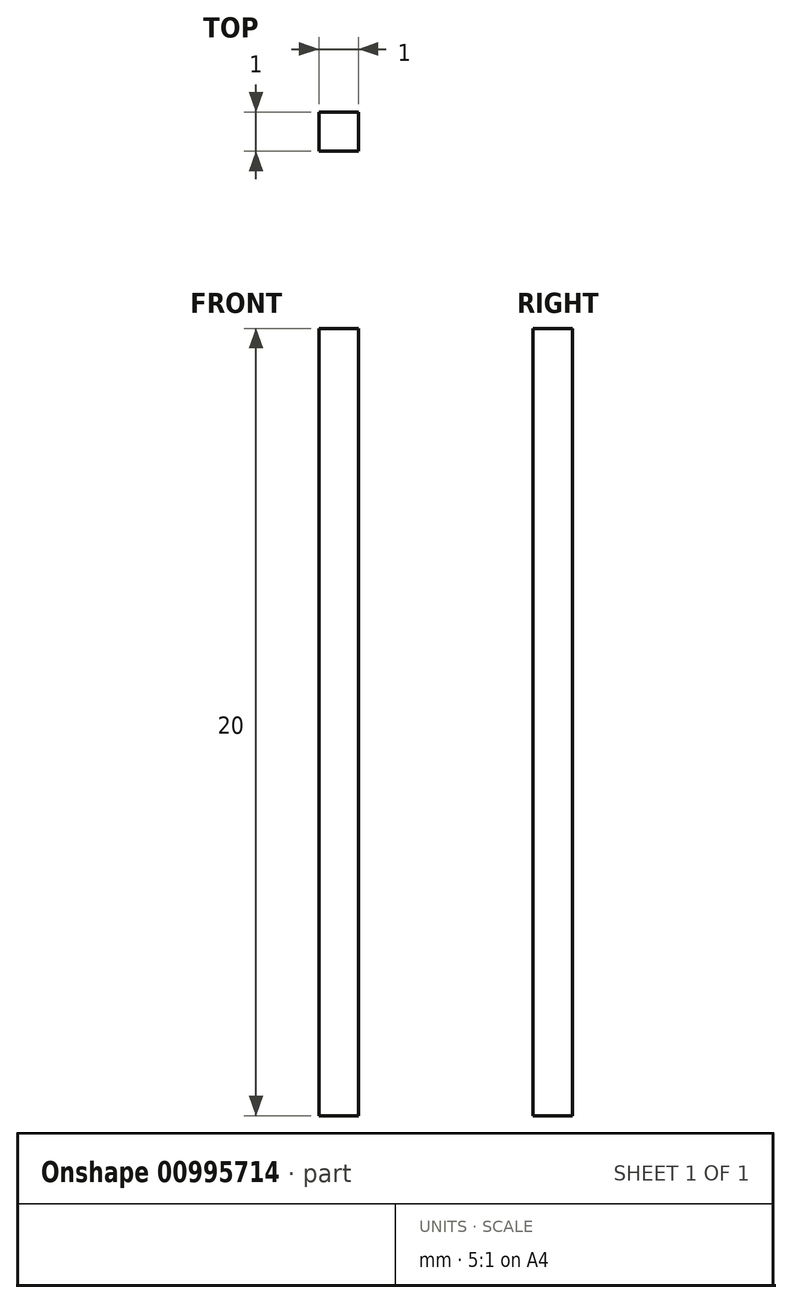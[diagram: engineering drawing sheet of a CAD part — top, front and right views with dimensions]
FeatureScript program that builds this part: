
annotation { "Feature Type Name" : "Feature", "Feature Type Description" : "" }
export const myFeature = defineFeature(function(context is Context, id is Id, definition is map)
    precondition{}
    {
        {
            var Q0;
            Q0=qCreatedBy(makeId("Top.planeOp"),FACE);
            var sketch = newSketch(context, id + "F0", { "sketchPlane" : qUnion([Q0])});
            skLineSegment(sketch, "E0.bottom", {"start": v(-0.5, -0.5) * mm, "end": v(0.5, -0.5) * mm});
            skLineSegment(sketch, "E0.top", {"start": v(-0.5, 0.5) * mm, "end": v(0.5, 0.5) * mm});
            skLineSegment(sketch, "E0.left", {"start": v(-0.5, -0.5) * mm, "end": v(-0.5, 0.5) * mm});
            skLineSegment(sketch, "E0.right", {"start": v(0.5, -0.5) * mm, "end": v(0.5, 0.5) * mm});
            skSolve(sketch);
        }
        {
            var Q0;
            Q0=makeQuery(id+"F0.imprint","IMPRINT",FACE,{"disambiguationData":[TD([[makeQuery(id+"F0.imprint","IMPRINT",EDGE,{"derivedFrom":sQuery(id+"F0.wireOp",EDGE,"E0.bottom")}),1.0]])]});
            extrude(context, id + "F1", {"entities" : qUnion([Q0]), "depth" : 20 * mm, "offsetDistance" : 25 * mm});
        }
    });
